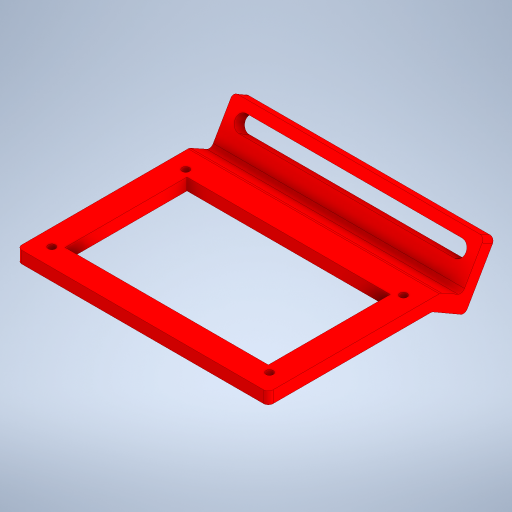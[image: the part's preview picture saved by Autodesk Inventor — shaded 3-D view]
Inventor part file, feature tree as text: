
AUTODESK INVENTOR PART (.ipt)
format: ipt  version: 2023 (Build 270158000, 158)  size: 341,504 bytes
history: native  units: mm
features: fillet x5, extrude x4, sketch x4
ambient origin geometry x8: Origin, YZ Plane, XZ Plane, XY Plane, X Axis, Y Axis, Z Axis, Center Point
bodies: Solid1 (feature_tree)
feature tree (13):
  extrude  "Extrusion1"  Depth=51.0mm
  extrude  "Extrusion2"  Depth=10.0mm
  extrude  "Extrusion3"  Depth=5.0mm TaperAngle=0.0deg
  extrude  "Extrusion4"  Depth=2.0mm
  fillet  "Fillet2"  Radius=3.0mm
  fillet  "Fillet3"  [1 undecoded]
  fillet  "Fillet4"  Radius=13.0mm
  fillet  "Fillet5"  Radius=105.0mm
  fillet  "Fillet6"  Radius=6.5mm
  sketch  "Sketch1"  dims[d0=85.0mm d1=51.0mm]
  sketch  "Sketch2"  dims[d2=20.0mm d3=10.0mm]
  sketch  "Sketch3"  dims[d4=10.0mm d5=5.0mm d6=0.0mm]
  sketch  "Sketch4"  dims[d13=2.5mm d14=3.0mm d15=3.0mm d16=30.0deg d18=13.0mm d19=105.0mm d20=0.0mm d21=6.5mm d22=90.0mm d23=7.0mm d24=0.0mm d25=0.0mm d26=5.0mm d28=9.0mm d29=0.0mm d30=0.0mm d31=5.0mm d32=2.0mm d33=45.0mm d34=10.0mm d37=25.0mm d38=2.0mm d39=2.0mm d40=2.0mm]
note: 1 required parameter value undecoded (feature->parameter linkage not recoverable at this tier; creation-order binding heuristic only, values carry confidence <= 0.55)
